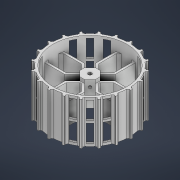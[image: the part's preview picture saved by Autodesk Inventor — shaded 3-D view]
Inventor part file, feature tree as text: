
AUTODESK INVENTOR PART (.ipt)
format: ipt  version: 2021 (Build 250183000, 183)  size: 1,137,664 bytes
history: native  units: mm
features: extrude x6, other x4, pattern_circular x2, sketch x2, plane x1, hole x1
ambient origin geometry x8: Origin, YZ Plane, XZ Plane, XY Plane, X Axis, Y Axis, Z Axis, Center Point
bodies: Volumenkörper1 (feature_tree)
feature tree (16):
  other  "Grundskizze"
  extrude  "Außenrahmen"  Depth=3.0mm
  extrude  "Radnabe"  Depth=2.0mm
  other  "Profilskizze"
  extrude  "Streben"  TaperAngle=45.0deg  [1 undecoded]
  extrude  "Profil"  TaperAngle=135.0deg  [1 undecoded]
  pattern_circular  "Runde Anordnung1"  [2 undecoded]
  other  "Einpresssmutter_skizze"
  other  "Einpressmutter_skizze2"
  plane  "Arbeitsebene2"
  extrude  "Extrusion13"  Depth=2.0mm
  pattern_circular  "Runde Anordnung4"  [2 undecoded]
  extrude  "Extrusion14"  Depth=35.0mm TaperAngle=0.0deg
  hole  "Bohrung1"  [1 undecoded]
  sketch  "Skizze9"  dims[d0=110.0mm d1=3.0mm]
  sketch  "Skizze10"  dims[d2=9.0mm d7=15.0mm d8=45.0deg d10=135.0deg d11=3.0mm d12=3.0mm d17=45.0mm d18=15.0mm d19=0.0mm d20=0.0mm d21=35.0mm d22=0.0mm d50=40.0mm d52=360.0deg d54=30.0mm d55=0.0mm d58=0.5mm d59=60.0mm d60=0.0mm d61=200.0mm d62=360.0deg d64=4.0mm d65=3.0mm d71=4.5mm d72=7.119163mm d75=4.5mm d78=1.5mm d79=2.5mm d88=5.0mm d89=40.0mm d91=360.0deg d93=7.118079mm d107=25.0mm d108=7.5mm d109=25.0mm d110=7.5mm d111=3.5mm d112=3.5mm d113=20.0mm d115=17.0mm d116=10.0mm d118=10.0mm d120=20.0mm d122=17.0mm d123=10.0mm d125=10.0mm d127=16.0mm d128=0.0mm d129=40.0mm d130=360.0deg d132=5.3mm d133=0.6mm d134=25.0mm d135=0.0mm d136=4.0mm d137=6.0mm d138=4.0mm d139=2.0mm d140=90.0deg d141=8.0mm d142=20.594885mm d73=0.5mm d74=0.872665mm]
note: 7 required parameter values undecoded (feature->parameter linkage not recoverable at this tier; creation-order binding heuristic only, values carry confidence <= 0.55)
